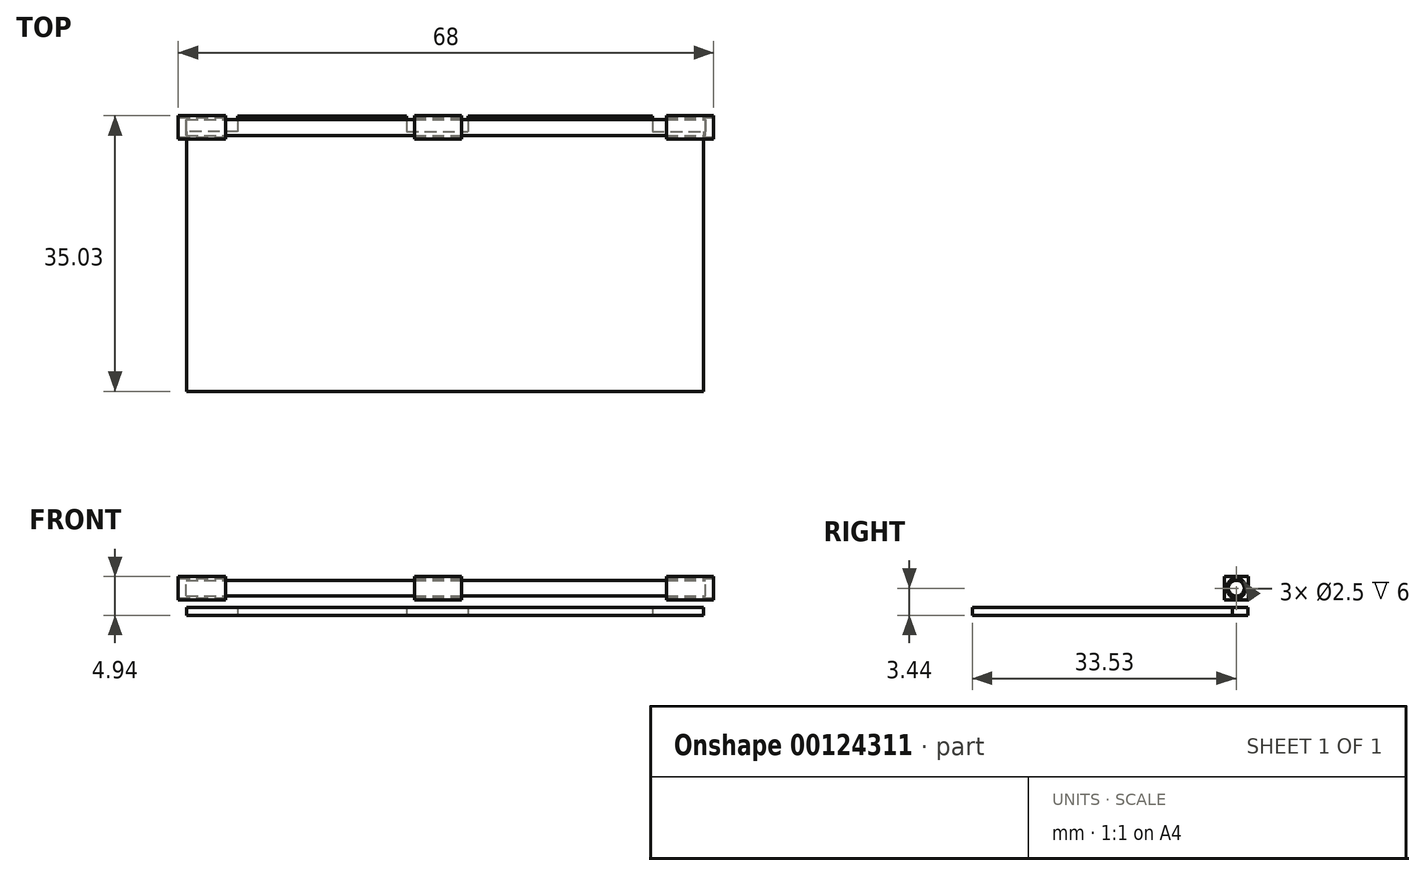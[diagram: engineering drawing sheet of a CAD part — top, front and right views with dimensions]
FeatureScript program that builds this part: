
annotation { "Feature Type Name" : "Feature", "Feature Type Description" : "" }
export const myFeature = defineFeature(function(context is Context, id is Id, definition is map)
    precondition{}
    {
        {
            var Q0;
            Q0=qCreatedBy(makeId("Top.planeOp"),FACE);
            var sketch = newSketch(context, id + "F0", { "sketchPlane" : qUnion([Q0])});
            skPoint(sketch, "E0", {"position": v(0, 0) * mm});
            skLineSegment(sketch, "E1.bottom", {"start": v(0, 0) * mm, "end": v(6, 0) * mm});
            skLineSegment(sketch, "E1.top", {"start": v(0, -3) * mm, "end": v(6, -3) * mm});
            skLineSegment(sketch, "E1.left", {"start": v(0, 0) * mm, "end": v(0, -3) * mm});
            skLineSegment(sketch, "E1.right", {"start": v(6, 0) * mm, "end": v(6, -3) * mm});
            skSolve(sketch);
        }
        {
            var Q0;
            Q0=makeQuery(id+"F0.imprint","IMPRINT",FACE,{"disambiguationData":[TD([[makeQuery(id+"F0.imprint","IMPRINT",EDGE,{"derivedFrom":sQuery(id+"F0.wireOp",EDGE,"E1.bottom")}),-1.0]])]});
            extrude(context, id + "F1", {"entities" : qUnion([Q0]), "depth" : 3 * mm, "offsetDistance" : 25 * mm});
        }
        {
            var Q0;
            Q0=makeQuery(id+"F1.opExtrude","SWEPT_FACE",FACE,{"disambiguationData":[OSD([sQuery(id+"F0.wireOp",EDGE,"E1.right")])]});
            var sketch = newSketch(context, id + "F2", { "sketchPlane" : qUnion([Q0])});
            skPoint(sketch, "E2", {"position": v(-1.5, 1.5) * mm});
            skPoint(sketch, "E2.positionSnap0", {"position": v(-3, 1.5) * mm});
            skPoint(sketch, "E2.positionSnap1", {"position": v(-1.5, 0) * mm});
            skSolve(sketch);
        }
        {
            var Q0;
            Q0=sQuery(id+"F2.wireOp",VERTEX,"E2");
            var Q1;
            Q1=makeQuery(id+"F1.opExtrude","SWEPT_BODY",BODY,{"disambiguationData":[OSD([sQuery(id+"F0.wireOp",EDGE,"E1.bottom"),sQuery(id+"F0.wireOp",EDGE,"E1.top"),sQuery(id+"F0.wireOp",EDGE,"E1.left"),sQuery(id+"F0.wireOp",EDGE,"E1.right")])]});
            hole(context, id + "F3", {"style" : HoleStyle.SIMPLE, "endStyle" : HoleEndStyle.THROUGH, "holeDiameter" : 2.5 * mm, "majorDiameter" : 5 * mm, "isTappedThrough" : true, "tappedDepth" : 12 * mm, "tapClearance" : 3, "startFromSketch" : true, "locations" : qUnion([Q0]), "scope" : qUnion([Q1])});
        }
        {
            var Q0;
            Q0=makeQuery(id+"F1.opExtrude","SWEPT_BODY",BODY,{"disambiguationData":[OSD([sQuery(id+"F0.wireOp",EDGE,"E1.bottom"),sQuery(id+"F0.wireOp",EDGE,"E1.top"),sQuery(id+"F0.wireOp",EDGE,"E1.left"),sQuery(id+"F0.wireOp",EDGE,"E1.right")])]});
            transform(context, id + "F4", {"entities" : qUnion([Q0]), "transformType" : TransformType.COPY});
        }
        {
            var Q0;
            Q0=makeQuery(id+"F4.opPattern","COPY",BODY,{"derivedFrom":makeQuery(id+"F1.opExtrude","SWEPT_BODY",BODY,{"disambiguationData":[OSD([sQuery(id+"F0.wireOp",EDGE,"E1.bottom"),sQuery(id+"F0.wireOp",EDGE,"E1.top"),sQuery(id+"F0.wireOp",EDGE,"E1.left"),sQuery(id+"F0.wireOp",EDGE,"E1.right")])]}),"instanceName":"1"});
            transform(context, id + "F5", {"entities" : qUnion([Q0]), "transformType" : TransformType.TRANSLATION_3D, "dx" : 31 * mm, "dy" : 0 * mm, "dz" : 0 * mm, "makeCopy" : false});
        }
        {
            var Q0;
            Q0=makeQuery(id+"F4.opPattern","COPY",BODY,{"derivedFrom":makeQuery(id+"F1.opExtrude","SWEPT_BODY",BODY,{"disambiguationData":[OSD([sQuery(id+"F0.wireOp",EDGE,"E1.bottom"),sQuery(id+"F0.wireOp",EDGE,"E1.top"),sQuery(id+"F0.wireOp",EDGE,"E1.left"),sQuery(id+"F0.wireOp",EDGE,"E1.right")])]}),"instanceName":"1"});
            transform(context, id + "F6", {"entities" : qUnion([Q0]), "transformType" : TransformType.COPY});
        }
        {
            var Q0;
            Q0=makeQuery(id+"F6.opPattern","COPY",BODY,{"derivedFrom":makeQuery(id+"F4.opPattern","COPY",BODY,{"derivedFrom":makeQuery(id+"F1.opExtrude","SWEPT_BODY",BODY,{"disambiguationData":[OSD([sQuery(id+"F0.wireOp",EDGE,"E1.bottom"),sQuery(id+"F0.wireOp",EDGE,"E1.top"),sQuery(id+"F0.wireOp",EDGE,"E1.left"),sQuery(id+"F0.wireOp",EDGE,"E1.right")])]}),"instanceName":"1"}),"instanceName":"1"});
            transform(context, id + "F7", {"entities" : qUnion([Q0]), "transformType" : TransformType.TRANSLATION_3D, "dx" : 31 * mm, "dy" : 0 * mm, "dz" : 0 * mm, "makeCopy" : false});
        }
        {
            var Q0;
            Q0=makeQuery(id+"F6.opPattern","COPY",FACE,{"derivedFrom":makeQuery(id+"F4.opPattern","COPY",FACE,{"derivedFrom":makeQuery(id+"F1.opExtrude","SWEPT_FACE",FACE,{"disambiguationData":[OSD([sQuery(id+"F0.wireOp",EDGE,"E1.right")])]}),"instanceName":"1"}),"instanceName":"1"});
            var sketch = newSketch(context, id + "F8", { "sketchPlane" : qUnion([Q0])});
            skCircle(sketch, "E3", {"center": v(-1.5, 1.5) * mm, "radius": 1 * mm});
            skSolve(sketch);
        }
        {
            var Q0;
            Q0=makeQuery(id+"F8.imprint","IMPRINT",FACE,{"disambiguationData":[TD([[makeQuery(id+"F8.imprint","IMPRINT",EDGE,{"derivedFrom":sQuery(id+"F8.wireOp",EDGE,"E3")}),1.0]])]});
            extrude(context, id + "F9", {"entities" : qUnion([Q0]), "oppositeDirection" : true, "depth" : 66 * mm, "offsetDistance" : 25 * mm});
        }
        {
            var Q0;
            Q0=makeQuery(id+"F1.opExtrude","SWEPT_BODY",BODY,{"disambiguationData":[OSD([sQuery(id+"F0.wireOp",EDGE,"E1.bottom"),sQuery(id+"F0.wireOp",EDGE,"E1.top"),sQuery(id+"F0.wireOp",EDGE,"E1.left"),sQuery(id+"F0.wireOp",EDGE,"E1.right")])]});
            transform(context, id + "F10", {"entities" : qUnion([Q0]), "transformType" : TransformType.TRANSLATION_3D, "dx" : 1 * mm, "dy" : 0 * mm, "dz" : 0 * mm, "makeCopy" : false});
        }
        {
            var Q0;
            Q0=makeQuery(id+"F6.opPattern","COPY",BODY,{"derivedFrom":makeQuery(id+"F4.opPattern","COPY",BODY,{"derivedFrom":makeQuery(id+"F1.opExtrude","SWEPT_BODY",BODY,{"disambiguationData":[OSD([sQuery(id+"F0.wireOp",EDGE,"E1.bottom"),sQuery(id+"F0.wireOp",EDGE,"E1.top"),sQuery(id+"F0.wireOp",EDGE,"E1.left"),sQuery(id+"F0.wireOp",EDGE,"E1.right")])]}),"instanceName":"1"}),"instanceName":"1"});
            transform(context, id + "F11", {"entities" : qUnion([Q0]), "transformType" : TransformType.TRANSLATION_3D, "dx" : 1 * mm, "dy" : 0 * mm, "dz" : 0 * mm, "makeCopy" : false});
        }
        {
            var Q0;
            Q0=qCreatedBy(makeId("Front.planeOp"),FACE);
            var sketch = newSketch(context, id + "F12", { "sketchPlane" : qUnion([Q0])});
            skPoint(sketch, "E4", {"position": v(8.57, 1.03) * mm});
            skLineSegment(sketch, "E5", {"start": v(8.57, 1.03) * mm, "end": v(8.57, -33.97) * mm});
            skLineSegment(sketch, "E6", {"start": v(8.57, -33.97) * mm, "end": v(30.7, -33.97) * mm});
            skLineSegment(sketch, "E7", {"start": v(8.57, -0.94) * mm, "end": v(2.1, -0.94) * mm});
            skLineSegment(sketch, "E8", {"start": v(2.1, -0.94) * mm, "end": v(2.1, -33.97) * mm});
            skLineSegment(sketch, "E9", {"start": v(2.1, -33.97) * mm, "end": v(8.57, -33.97) * mm});
            skLineSegment(sketch, "E10.MirrorCS", {"start": v(61.23, 1.03) * mm, "end": v(61.23, -33.97) * mm});
            skLineSegment(sketch, "E11.MirrorCS", {"start": v(61.23, -0.94) * mm, "end": v(67.72, -0.94) * mm});
            skLineSegment(sketch, "E12.MirrorCS", {"start": v(67.72, -0.94) * mm, "end": v(67.72, -33.97) * mm});
            skLineSegment(sketch, "E13.MirrorCS", {"start": v(67.72, -33.97) * mm, "end": v(61.23, -33.97) * mm});
            skLineSegment(sketch, "E14.MirrorCS", {"start": v(61.23, -33.97) * mm, "end": v(39.12, -33.97) * mm});
            skPoint(sketch, "E15", {"position": v(37.8, 1.03) * mm});
            skLineSegment(sketch, "E16", {"start": v(37.8, 1.03) * mm, "end": v(61.23, 1.03) * mm});
            skLineSegment(sketch, "E17", {"start": v(37.8, 1.03) * mm, "end": v(37.8, -33.97) * mm});
            skLineSegment(sketch, "E18", {"start": v(37.8, -33.97) * mm, "end": v(39.12, -33.97) * mm});
            skLineSegment(sketch, "E19", {"start": v(30.7, -33.97) * mm, "end": v(37.8, -33.97) * mm});
            skLineSegment(sketch, "E20", {"start": v(30.7, -0.94) * mm, "end": v(37.8, -0.94) * mm});
            skLineSegment(sketch, "E21", {"start": v(8.57, 1.03) * mm, "end": v(30.01, 1.03) * mm});
            skLineSegment(sketch, "E22", {"start": v(30.01, 1.03) * mm, "end": v(30.01, -33.97) * mm});
            skLineSegment(sketch, "E23", {"start": v(30.7, -0.94) * mm, "end": v(30.01, -0.94) * mm});
            skSolve(sketch);
        }
        {
            var Q0;
            {var subQ2=sQuery(id+"F12.wireOp",EDGE,"E7");Q0=makeQuery(id+"F12.imprint","IMPRINT",FACE,{"disambiguationData":[TD([[makeQuery(id+"F12.imprint","IMPRINT",EDGE,{"derivedFrom":subQ2}),1.0]])]});}
            var Q1;
            {var subQ3=sQuery(id+"F12.wireOp",EDGE,"wXIJUId7-63zh-X2BZ-qiSm-aVDhm0krV6B3");Q1=makeQuery(id+"F12.imprint","IMPRINT",FACE,{"disambiguationData":[TD([[makeQuery(id+"F12.imprint","IMPRINT",EDGE,{"derivedFrom":subQ3}),-1.0]])]});}
            var Q2;
            {var subQ0=sQuery(id+"F12.wireOp",EDGE,"E19");Q2=makeQuery(id+"F12.imprint","IMPRINT",FACE,{"disambiguationData":[TD([[makeQuery(id+"F12.imprint","IMPRINT",EDGE,{"derivedFrom":subQ0}),1.0]])]});}
            var Q3;
            {var subQ1=sQuery(id+"F12.wireOp",EDGE,"E14.MirrorCS");Q3=makeQuery(id+"F12.imprint","IMPRINT",FACE,{"disambiguationData":[TD([[makeQuery(id+"F12.imprint","IMPRINT",EDGE,{"derivedFrom":subQ1}),-1.0]])]});}
            var Q4;
            {var subQ2=sQuery(id+"F12.wireOp",EDGE,"E11.MirrorCS");Q4=makeQuery(id+"F12.imprint","IMPRINT",FACE,{"disambiguationData":[TD([[makeQuery(id+"F12.imprint","IMPRINT",EDGE,{"derivedFrom":subQ2}),-1.0]])]});}
            var Q5;
            {var subQ0=sQuery(id+"F12.wireOp",EDGE,"E21");Q5=makeQuery(id+"F12.imprint","IMPRINT",FACE,{"disambiguationData":[TD([[makeQuery(id+"F12.imprint","IMPRINT",EDGE,{"derivedFrom":subQ0}),-1.0]])]});}
            extrude(context, id + "F13", {"entities" : qUnion([Q0, Q1, Q2, Q3, Q4, Q5]), "depth" : 1 * mm, "offsetDistance" : 25 * mm});
        }
        {
            var Q0;
            Q0=makeQuery(id+"F13.opExtrude","SWEPT_BODY",BODY,{"disambiguationData":[OSD([sQuery(id+"F12.wireOp",EDGE,"E5"),sQuery(id+"F12.wireOp",EDGE,"E6"),sQuery(id+"F12.wireOp",EDGE,"E7"),sQuery(id+"F12.wireOp",EDGE,"E8"),sQuery(id+"F12.wireOp",EDGE,"E9"),sQuery(id+"F12.wireOp",EDGE,"E10.MirrorCS"),sQuery(id+"F12.wireOp",EDGE,"E11.MirrorCS"),sQuery(id+"F12.wireOp",EDGE,"E12.MirrorCS"),sQuery(id+"F12.wireOp",EDGE,"E13.MirrorCS"),sQuery(id+"F12.wireOp",EDGE,"E14.MirrorCS"),sQuery(id+"F12.wireOp",EDGE,"E16"),sQuery(id+"F12.wireOp",EDGE,"E17"),sQuery(id+"F12.wireOp",EDGE,"E18"),sQuery(id+"F12.wireOp",EDGE,"E19"),sQuery(id+"F12.wireOp",EDGE,"E20"),sQuery(id+"F12.wireOp",EDGE,"E21"),sQuery(id+"F12.wireOp",EDGE,"E22"),sQuery(id+"F12.wireOp",EDGE,"E23")])]});
            transform(context, id + "F14", {"entities" : qUnion([Q0]), "transformType" : TransformType.TRANSLATION_3D, "dx" : 0 * mm, "dy" : -1 * mm, "dz" : 0 * mm, "makeCopy" : false});
        }
        {
            var Q0;
            Q0=makeQuery(id+"F13.opExtrude","SWEPT_BODY",BODY,{"disambiguationData":[OSD([sQuery(id+"F12.wireOp",EDGE,"E5"),sQuery(id+"F12.wireOp",EDGE,"E6"),sQuery(id+"F12.wireOp",EDGE,"E7"),sQuery(id+"F12.wireOp",EDGE,"E8"),sQuery(id+"F12.wireOp",EDGE,"E9"),sQuery(id+"F12.wireOp",EDGE,"E10.MirrorCS"),sQuery(id+"F12.wireOp",EDGE,"E11.MirrorCS"),sQuery(id+"F12.wireOp",EDGE,"E12.MirrorCS"),sQuery(id+"F12.wireOp",EDGE,"E13.MirrorCS"),sQuery(id+"F12.wireOp",EDGE,"E14.MirrorCS"),sQuery(id+"F12.wireOp",EDGE,"E16"),sQuery(id+"F12.wireOp",EDGE,"E17"),sQuery(id+"F12.wireOp",EDGE,"E18"),sQuery(id+"F12.wireOp",EDGE,"E19"),sQuery(id+"F12.wireOp",EDGE,"E20"),sQuery(id+"F12.wireOp",EDGE,"E21"),sQuery(id+"F12.wireOp",EDGE,"E22"),sQuery(id+"F12.wireOp",EDGE,"E23")])]});
            var Q1;
            Q1=makeQuery(id+"F13.opExtrude","CAP_EDGE",EDGE,{"disambiguationData":[OSD([sQuery(id+"F12.wireOp",EDGE,"E20"),sQuery(id+"F12.wireOp",EDGE,"E23")])],"isStart":false});
            transform(context, id + "F15", {"entities" : qUnion([Q0]), "transformType" : TransformType.ROTATION, "transformAxis" : qUnion([Q1]), "angle" : 270 * degree, "makeCopy" : false});
        }
    });
